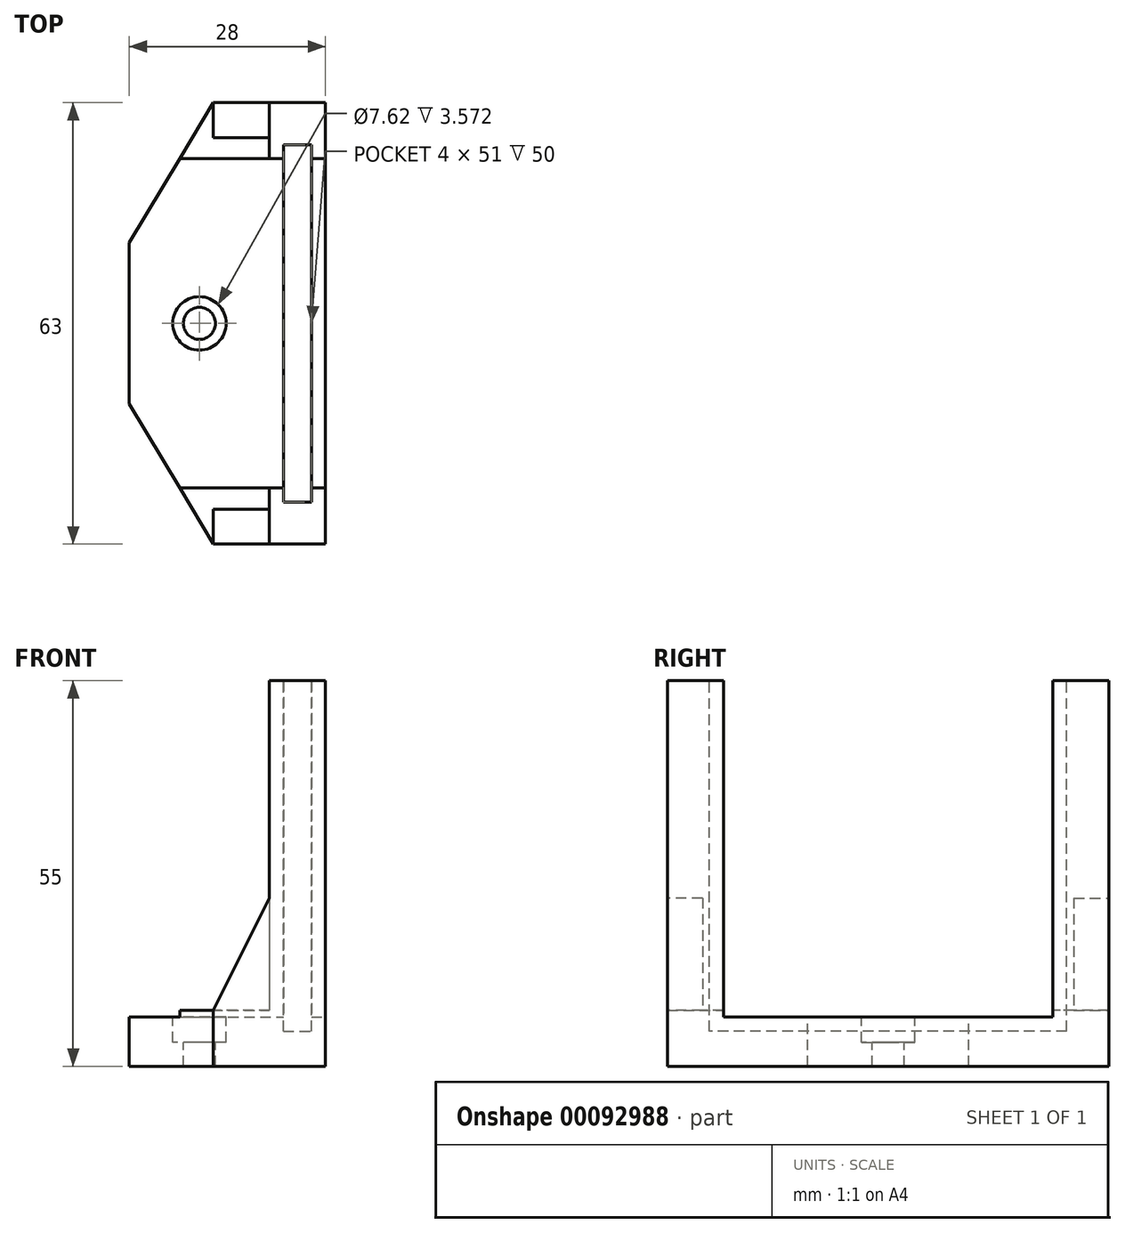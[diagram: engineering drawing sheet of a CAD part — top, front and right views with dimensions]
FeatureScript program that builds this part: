
annotation { "Feature Type Name" : "Feature", "Feature Type Description" : "" }
export const myFeature = defineFeature(function(context is Context, id is Id, definition is map)
    precondition{}
    {
        {
            var Q0;
            Q0=qCreatedBy(makeId("Top.planeOp"),FACE);
            var sketch = newSketch(context, id + "F0", { "sketchPlane" : qUnion([Q0])});
            skLineSegment(sketch, "E0.bottom", {"start": v(10, 31.5) * mm, "end": v(-10, 31.5) * mm});
            skLineSegment(sketch, "E0.top", {"start": v(10, -31.5) * mm, "end": v(-10, -31.5) * mm});
            skLineSegment(sketch, "E0.left", {"start": v(10, 31.5) * mm, "end": v(10, -31.5) * mm});
            skLineSegment(sketch, "E0.right", {"start": v(-10, 31.5) * mm, "end": v(-10, -31.5) * mm});
            skPoint(sketch, "E0.middle", {"position": v(0, 0) * mm});
            skSolve(sketch);
        }
        {
            var Q0;
            Q0=qSketchRegion(id+"F0",true);
            extrude(context, id + "F1", {"entities" : qUnion([Q0]), "depth" : 8 * mm});
        }
        {
            var Q0;
            Q0=makeQuery(id+"F1.opExtrude","SWEPT_FACE",FACE,{"disambiguationData":[OSD([sQuery(id+"F0.wireOp",EDGE,"E0.left")])]});
            var sketch = newSketch(context, id + "F2", { "sketchPlane" : qUnion([Q0])});
            skLineSegment(sketch, "E1.bottom", {"start": v(-31.5, 0) * mm, "end": v(31.5, 0) * mm});
            skLineSegment(sketch, "E1.top", {"start": v(-31.5, 55) * mm, "end": v(31.5, 55) * mm});
            skLineSegment(sketch, "E1.left", {"start": v(-31.5, 0) * mm, "end": v(-31.5, 55) * mm});
            skLineSegment(sketch, "E1.right", {"start": v(31.5, 0) * mm, "end": v(31.5, 55) * mm});
            skSolve(sketch);
        }
        {
            var Q0;
            Q0=qSketchRegion(id+"F2",true);
            var Q1;
            Q1=qSketchRegion(id+"F4",true);
            extrude(context, id + "F3", {"entities" : qUnion([Q0, Q1]), "operationType" : NewBodyOperationType.ADD, "depth" : 8 * mm});
        }
        {
            var Q0;
            Q0=makeQuery(id+"F1.opExtrude","CAP_FACE",FACE,{"disambiguationData":[OSD([sQuery(id+"F0.wireOp",EDGE,"E0.bottom"),sQuery(id+"F0.wireOp",EDGE,"E0.top"),sQuery(id+"F0.wireOp",EDGE,"E0.left"),sQuery(id+"F0.wireOp",EDGE,"E0.right")])],"isStart":false});
            var sketch = newSketch(context, id + "F4", { "sketchPlane" : qUnion([Q0])});
            skPoint(sketch, "E2", {"position": v(0, 0) * mm});
            skSolve(sketch);
        }
        {
            var Q0;
            Q0=sQuery(id+"F4.wireOp",VERTEX,"E2");
            var Q1;
            Q1=makeQuery(id+"F1.opExtrude","SWEPT_BODY",BODY,{"disambiguationData":[OSD([sQuery(id+"F0.wireOp",EDGE,"E0.bottom"),sQuery(id+"F0.wireOp",EDGE,"E0.top"),sQuery(id+"F0.wireOp",EDGE,"E0.left"),sQuery(id+"F0.wireOp",EDGE,"E0.right")])]});
            hole(context, id + "F5", {"style" : HoleStyle.C_BORE, "endStyle" : HoleEndStyle.THROUGH, "holeDiameter" : 0.18 * 25.4 * mm, "cBoreDiameter" : 0.3 * 25.4 * mm, "cBoreDepth" : 0.18 * 25.4 * mm, "locations" : qUnion([Q0]), "scope" : qUnion([Q1]), "isTappedThrough" : true});
        }
        {
            var Q0;
            Q0=makeQuery(id+"F3.opExtrude","CAP_FACE",FACE,{"disambiguationData":[OSD([sQuery(id+"F2.wireOp",EDGE,"E1.bottom"),sQuery(id+"F2.wireOp",EDGE,"E1.top"),sQuery(id+"F2.wireOp",EDGE,"E1.left"),sQuery(id+"F2.wireOp",EDGE,"E1.right")])],"isStart":false});
            var sketch = newSketch(context, id + "F6", { "sketchPlane" : qUnion([Q0])});
            skLineSegment(sketch, "E3.bottom", {"start": v(-23.5, 55) * mm, "end": v(23.5, 55) * mm});
            skLineSegment(sketch, "E3.top", {"start": v(-23.5, 7) * mm, "end": v(23.5, 7) * mm});
            skLineSegment(sketch, "E3.left", {"start": v(-23.5, 55) * mm, "end": v(-23.5, 7) * mm});
            skLineSegment(sketch, "E3.right", {"start": v(23.5, 55) * mm, "end": v(23.5, 7) * mm});
            skSolve(sketch);
        }
        {
            var Q0;
            Q0=makeQuery(id+"F6.imprint","IMPRINT",FACE,{"disambiguationData":[TD([[makeQuery(id+"F6.imprint","IMPRINT",EDGE,{"derivedFrom":sQuery(id+"F6.wireOp",EDGE,"E3.bottom")}),-1.0]])]});
            extrude(context, id + "F7", {"entities" : qUnion([Q0]), "operationType" : NewBodyOperationType.REMOVE, "endBound" : BoundingType.THROUGH_ALL, "oppositeDirection" : true, "depth" : 25 * mm});
        }
        {
            var Q0;
            Q0=makeQuery(id+"F3.opExtrude","CAP_VERTEX",VERTEX,{"disambiguationData":[OSD([sQuery(id+"F2.wireOp",EDGE,"E1.top"),sQuery(id+"F2.wireOp",EDGE,"E1.right")])],"isStart":false});
            var Q1;
            Q1=makeQuery(id+"F7.boolean.opBoolean","INTERSECT",VERTEX,{"disambiguationData":[OD(1.0)],"derivedFrom":[makeQuery(id+"F3.opExtrude","CAP_FACE",FACE,{"disambiguationData":[OSD([sQuery(id+"F2.wireOp",EDGE,"E1.bottom"),sQuery(id+"F2.wireOp",EDGE,"E1.top"),sQuery(id+"F2.wireOp",EDGE,"E1.left"),sQuery(id+"F2.wireOp",EDGE,"E1.right")])],"isStart":true}),makeQuery(id+"F7.opExtrude","SWEPT_FACE",FACE,{"disambiguationData":[OSD([sQuery(id+"F6.wireOp",EDGE,"E3.right")])]})]});
            var Q2;
            Q2=makeQuery(id+"F3.opExtrude","CAP_VERTEX",VERTEX,{"disambiguationData":[OSD([sQuery(id+"F2.wireOp",EDGE,"E1.top"),sQuery(id+"F2.wireOp",EDGE,"E1.left")])],"isStart":false});
            cPlane(context, id + "F8", {"entities" : qUnion([Q0, Q1, Q2]), "cplaneType" : CPlaneType.THREE_POINT, "offset" : 150 * mm, "width" : 150 * mm, "height" : 150 * mm});
        }
        {
            var Q0;
            Q0=qCreatedBy(id+"F8.planeOp",FACE);
            var sketch = newSketch(context, id + "F9", { "sketchPlane" : qUnion([Q0])});
            skLineSegment(sketch, "E4.bottom", {"start": v(12, -25.5) * mm, "end": v(16, -25.5) * mm});
            skLineSegment(sketch, "E4.top", {"start": v(12, 25.5) * mm, "end": v(16, 25.5) * mm});
            skLineSegment(sketch, "E4.left", {"start": v(12, -25.5) * mm, "end": v(12, 25.5) * mm});
            skLineSegment(sketch, "E4.right", {"start": v(16, -25.5) * mm, "end": v(16, 25.5) * mm});
            skSolve(sketch);
        }
        {
            var Q0;
            Q0=makeQuery(id+"F9.imprint","IMPRINT",FACE,{"disambiguationData":[TD([[makeQuery(id+"F9.imprint","IMPRINT",EDGE,{"derivedFrom":sQuery(id+"F9.wireOp",EDGE,"E4.bottom")}),1.0]])]});
            extrude(context, id + "F10", {"entities" : qUnion([Q0]), "operationType" : NewBodyOperationType.REMOVE, "depth" : 50 * mm});
        }
        {
            var Q0;
            Q0=makeQuery(id+"F3.boolean.opBoolean","MERGE",FACE,{"derivedFrom":[makeQuery(id+"F1.opExtrude","SWEPT_FACE",FACE,{"disambiguationData":[OSD([sQuery(id+"F0.wireOp",EDGE,"E0.top")])]}),makeQuery(id+"F3.opExtrude","SWEPT_FACE",FACE,{"disambiguationData":[OSD([sQuery(id+"F2.wireOp",EDGE,"E1.left")])]})]});
            var sketch = newSketch(context, id + "F11", { "sketchPlane" : qUnion([Q0])});
            skLineSegment(sketch, "E5", {"start": v(10, 8) * mm, "end": v(2, 8) * mm});
            skLineSegment(sketch, "E6", {"start": v(2, 8) * mm, "end": v(10, 24) * mm});
            skLineSegment(sketch, "E7", {"start": v(10, 24) * mm, "end": v(10, 8) * mm});
            skSolve(sketch);
        }
        {
            var Q0;
            Q0=qSketchRegion(id+"F11",true);
            extrude(context, id + "F12", {"entities" : qUnion([Q0]), "operationType" : NewBodyOperationType.ADD, "oppositeDirection" : true, "depth" : 5 * mm});
        }
        {
            var Q0;
            Q0=makeQuery(id+"F3.boolean.opBoolean","MERGE",FACE,{"derivedFrom":[makeQuery(id+"F1.opExtrude","SWEPT_FACE",FACE,{"disambiguationData":[OSD([sQuery(id+"F0.wireOp",EDGE,"E0.bottom")])]}),makeQuery(id+"F3.opExtrude","SWEPT_FACE",FACE,{"disambiguationData":[OSD([sQuery(id+"F2.wireOp",EDGE,"E1.right")])]})]});
            var sketch = newSketch(context, id + "F13", { "sketchPlane" : qUnion([Q0])});
            skLineSegment(sketch, "E8", {"start": v(-10, 8) * mm, "end": v(-2, 8) * mm});
            skLineSegment(sketch, "E9", {"start": v(-2, 8) * mm, "end": v(-10, 24) * mm});
            skLineSegment(sketch, "E10", {"start": v(-10, 24) * mm, "end": v(-10, 8) * mm});
            skSolve(sketch);
        }
        {
            var Q0;
            Q0=qSketchRegion(id+"F13",true);
            extrude(context, id + "F14", {"entities" : qUnion([Q0]), "operationType" : NewBodyOperationType.ADD, "oppositeDirection" : true, "depth" : 5 * mm});
        }
        {
            var Q0;
            {var subQ0=sQuery(id+"F0.wireOp",EDGE,"E0.right");var subQ1=sQuery(id+"F0.wireOp",EDGE,"E0.top");var subQ4=sQuery(id+"F0.wireOp",EDGE,"E0.bottom");Q0=makeQuery(id+"F10.boolean.opBoolean","SPLIT",FACE,{"disambiguationData":[TD([makeQuery(id+"F1.opExtrude","SWEPT_FACE",FACE,{"disambiguationData":[OSD([subQ4])]})])],"derivedFrom":makeQuery(id+"F7.boolean.opBoolean","MERGE",FACE,{"derivedFrom":[makeQuery(id+"F1.opExtrude","CAP_FACE",FACE,{"disambiguationData":[OSD([subQ4,subQ1,sQuery(id+"F0.wireOp",EDGE,"E0.left"),subQ0])],"isStart":false}),makeQuery(id+"F7.opExtrude","SWEPT_FACE",FACE,{"disambiguationData":[OSD([sQuery(id+"F6.wireOp",EDGE,"E3.top")])]})]})});}
            var sketch = newSketch(context, id + "F15", { "sketchPlane" : qUnion([Q0])});
            skLineSegment(sketch, "E11", {"start": v(2, 31.5) * mm, "end": v(-10, 11.5) * mm});
            skLineSegment(sketch, "E12", {"start": v(-10, 11.5) * mm, "end": v(-10, 31.5) * mm});
            skLineSegment(sketch, "E13", {"start": v(-10, 31.5) * mm, "end": v(2, 31.5) * mm});
            skLineSegment(sketch, "E14.MirrorCS", {"start": v(-10, -31.5) * mm, "end": v(2, -31.5) * mm});
            skLineSegment(sketch, "E15.MirrorCS", {"start": v(-10, -11.5) * mm, "end": v(-10, -31.5) * mm});
            skLineSegment(sketch, "E16.MirrorCS", {"start": v(2, -31.5) * mm, "end": v(-10, -11.5) * mm});
            skSolve(sketch);
        }
        {
            var Q0;
            Q0=qSketchRegion(id+"F15",true);
            extrude(context, id + "F16", {"entities" : qUnion([Q0]), "operationType" : NewBodyOperationType.REMOVE, "oppositeDirection" : true, "depth" : 25 * mm});
        }
    });
